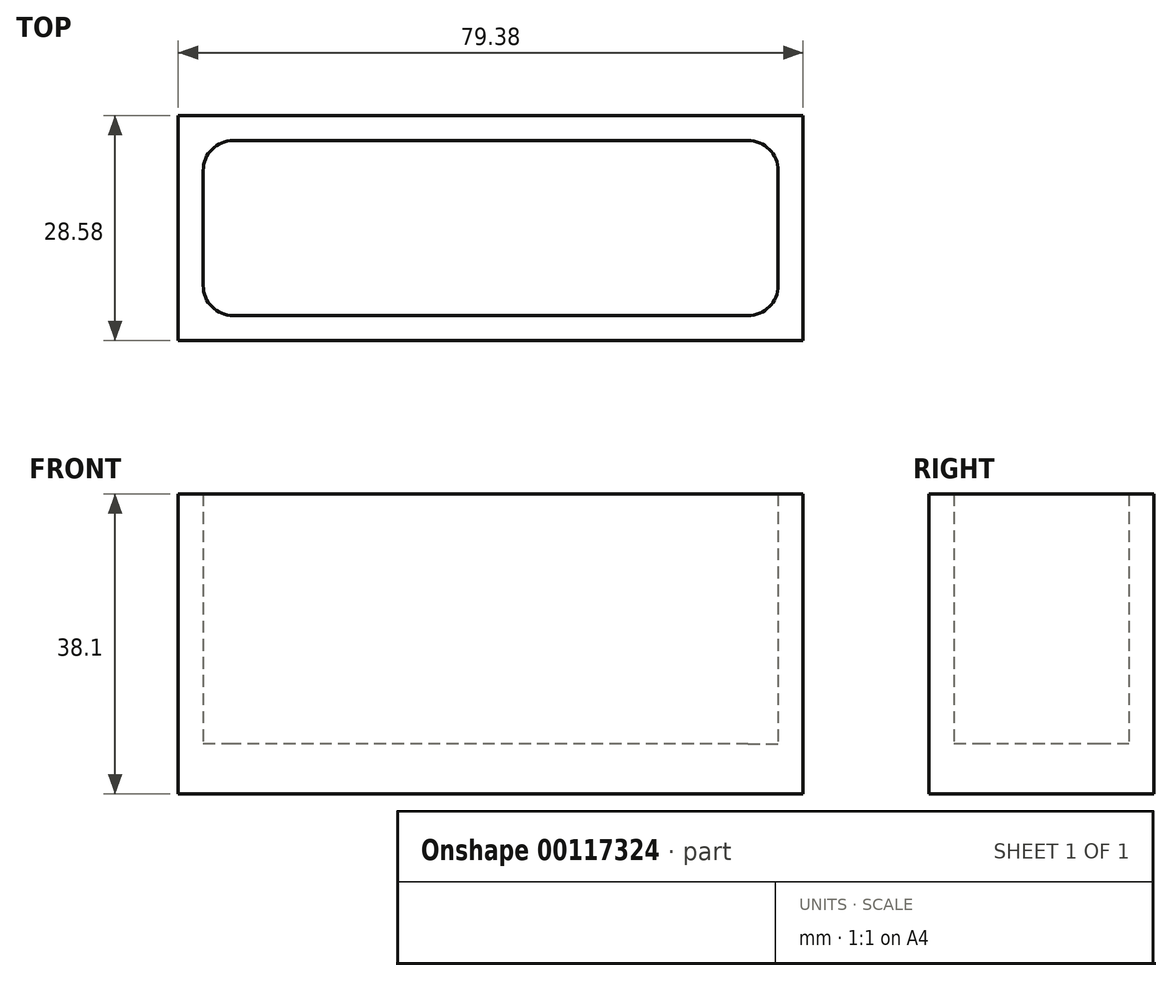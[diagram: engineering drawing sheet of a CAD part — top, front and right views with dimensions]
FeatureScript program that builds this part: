
annotation { "Feature Type Name" : "Feature", "Feature Type Description" : "" }
export const myFeature = defineFeature(function(context is Context, id is Id, definition is map)
    precondition{}
    {
        {
            var Q0;
            Q0=qCreatedBy(makeId("Top.planeOp"),FACE);
            var sketch = newSketch(context, id + "F0", { "sketchPlane" : qUnion([Q0])});
            skLineSegment(sketch, "E0.bottom", {"start": v(39.69, 14.29) * mm, "end": v(-39.69, 14.29) * mm});
            skLineSegment(sketch, "E0.top", {"start": v(39.69, -14.29) * mm, "end": v(-39.69, -14.29) * mm});
            skLineSegment(sketch, "E0.left", {"start": v(39.69, 14.29) * mm, "end": v(39.69, -14.29) * mm});
            skLineSegment(sketch, "E0.right", {"start": v(-39.69, 14.29) * mm, "end": v(-39.69, -14.29) * mm});
            skPoint(sketch, "E0.middle", {"position": v(0, 0) * mm});
            skSolve(sketch);
        }
        {
            var Q0;
            Q0 = qSketchRegion(id + "F0", true);
            extrude(context, id + "F1", {"entities" : qUnion([Q0]), "depth" : 6.35 * mm});
        }
        {
            var Q0;
            Q0=makeQuery(id+"F1.opExtrude","CAP_FACE",FACE,{"disambiguationData":[OSD([sQuery(id+"F0.wireOp",EDGE,"E0.bottom"),sQuery(id+"F0.wireOp",EDGE,"E0.top"),sQuery(id+"F0.wireOp",EDGE,"E0.left"),sQuery(id+"F0.wireOp",EDGE,"E0.right")])],"isStart":false});
            var sketch = newSketch(context, id + "F2", { "sketchPlane" : qUnion([Q0])});
            skLineSegment(sketch, "E1.bottom", {"start": v(39.69, 14.29) * mm, "end": v(-39.69, 14.29) * mm});
            skLineSegment(sketch, "E1.top", {"start": v(39.69, -14.29) * mm, "end": v(-39.69, -14.29) * mm});
            skLineSegment(sketch, "E1.left", {"start": v(39.69, 14.29) * mm, "end": v(39.69, -14.29) * mm});
            skLineSegment(sketch, "E1.right", {"start": v(-39.69, 14.29) * mm, "end": v(-39.69, -14.29) * mm});
            skPoint(sketch, "E1.middle", {"position": v(0, 0) * mm});
            skLineSegment(sketch, "E2.bottom", {"start": v(36.51, 11.11) * mm, "end": v(-36.51, 11.11) * mm});
            skLineSegment(sketch, "E2.top", {"start": v(36.51, -11.11) * mm, "end": v(-36.51, -11.11) * mm});
            skLineSegment(sketch, "E2.left", {"start": v(36.51, 11.11) * mm, "end": v(36.51, -11.11) * mm});
            skLineSegment(sketch, "E2.right", {"start": v(-36.51, 11.11) * mm, "end": v(-36.51, -11.11) * mm});
            skSolve(sketch);
        }
        {
            var Q0;
            Q0 = qSketchRegion(id + "F2", true);
            extrude(context, id + "F3", {"entities" : qUnion([Q0]), "operationType" : NewBodyOperationType.ADD, "depth" : 31.75 * mm});
        }
        {
            var Q0;
            Q0=makeQuery(id+"F3.opExtrude","CAP_EDGE",EDGE,{"disambiguationData":[OSD([sQuery(id+"F2.wireOp",EDGE,"E2.top")])],"isStart":true});
            var Q1;
            Q1=makeQuery(id+"F3.opExtrude","CAP_EDGE",EDGE,{"disambiguationData":[OSD([sQuery(id+"F2.wireOp",EDGE,"E2.right")])],"isStart":true});
            var Q2;
            Q2=makeQuery(id+"F3.opExtrude","CAP_EDGE",EDGE,{"disambiguationData":[OSD([sQuery(id+"F2.wireOp",EDGE,"E2.bottom")])],"isStart":true});
            var Q3;
            Q3=makeQuery(id+"F3.opExtrude","CAP_EDGE",EDGE,{"disambiguationData":[OSD([sQuery(id+"F2.wireOp",EDGE,"E2.left")])],"isStart":true});
            var Q4;
            Q4=makeQuery(id+"F3.opExtrude","SWEPT_EDGE",EDGE,{"disambiguationData":[OSD([sQuery(id+"F2.wireOp",EDGE,"E2.bottom"),sQuery(id+"F2.wireOp",EDGE,"E2.left")])]});
            var Q5;
            Q5=makeQuery(id+"F3.opExtrude","SWEPT_EDGE",EDGE,{"disambiguationData":[OSD([sQuery(id+"F2.wireOp",EDGE,"E2.top"),sQuery(id+"F2.wireOp",EDGE,"E2.left")])]});
            var Q6;
            Q6=makeQuery(id+"F3.opExtrude","SWEPT_EDGE",EDGE,{"disambiguationData":[OSD([sQuery(id+"F2.wireOp",EDGE,"E2.top"),sQuery(id+"F2.wireOp",EDGE,"E2.right")])]});
            var Q7;
            Q7=makeQuery(id+"F3.opExtrude","SWEPT_EDGE",EDGE,{"disambiguationData":[OSD([sQuery(id+"F2.wireOp",EDGE,"E2.bottom"),sQuery(id+"F2.wireOp",EDGE,"E2.right")])]});
            fillet(context, id + "F4", {"entities" : qUnion([Q0, Q1, Q2, Q3, Q4, Q5, Q6, Q7]), "radius" : 3.8 * mm, "tangentPropagation" : true, "allowEdgeOverflow" : false});
        }
    });
